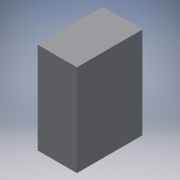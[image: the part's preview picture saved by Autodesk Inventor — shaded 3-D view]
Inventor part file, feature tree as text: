
AUTODESK INVENTOR PART (.ipt)
format: ipt  version: 2016 (Build 200138000, 138)  size: 83,456 bytes
history: native  units: in
note: dims shown in document units (in); Inventor stores cm internally (conversion verified against a paired STEP export)
features: extrude x1, sketch x1
ambient origin geometry x8: Origin, YZ Plane, XZ Plane, XY Plane, X Axis, Y Axis, Z Axis, Center Point
bodies: Solid1 (feature_tree)
feature tree (2):
  extrude  "Extrusion1"  Depth=2.5in
  sketch  "Sketch1"  dims[d0=1.5in d1=2.5in d2=3.5in d3=0.0in]
